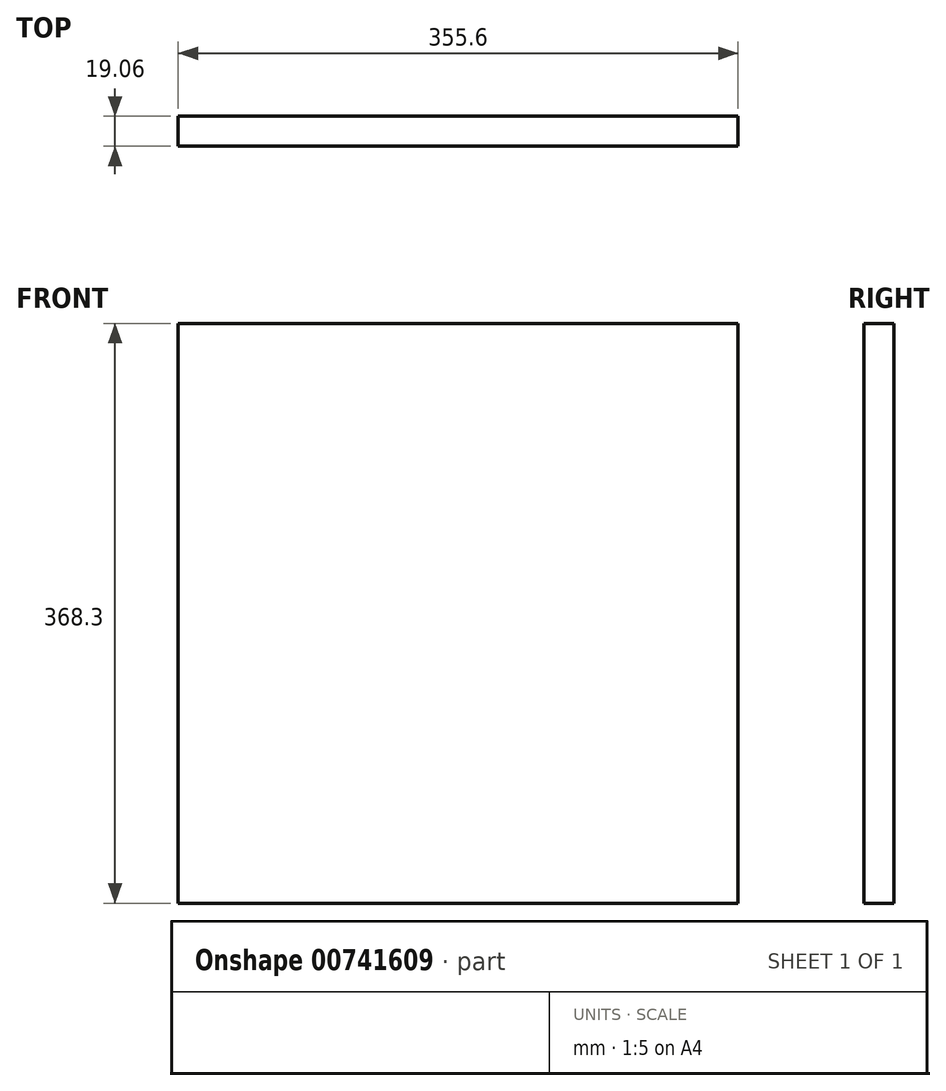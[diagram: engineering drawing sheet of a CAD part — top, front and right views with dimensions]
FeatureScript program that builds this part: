
annotation { "Feature Type Name" : "Feature", "Feature Type Description" : "" }
export const myFeature = defineFeature(function(context is Context, id is Id, definition is map)
    precondition{}
    {
        {
            var Q0;
            Q0=qCreatedBy(makeId("Right.planeOp"),FACE);
            var sketch = newSketch(context, id + "F0", { "sketchPlane" : qUnion([Q0])});
            skLineSegment(sketch, "E0.bottom", {"start": v(9.52, 184.15) * mm, "end": v(-9.53, 184.15) * mm});
            skLineSegment(sketch, "E0.top", {"start": v(9.53, -184.15) * mm, "end": v(-9.52, -184.15) * mm});
            skLineSegment(sketch, "E0.left", {"start": v(9.52, 184.15) * mm, "end": v(9.53, -184.15) * mm});
            skLineSegment(sketch, "E0.right", {"start": v(-9.53, 184.15) * mm, "end": v(-9.52, -184.15) * mm});
            skPoint(sketch, "E0.middle", {"position": v(0, 0) * mm});
            skSolve(sketch);
        }
        {
            var Q0;
            Q0 = qSketchRegion(id + "F0", true);
            extrude(context, id + "F1", {"entities" : qUnion([Q0]), "depth" : 355.6 * mm, "offsetDistance" : 25.4 * mm});
        }
    });
